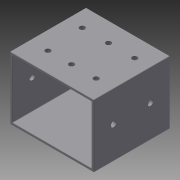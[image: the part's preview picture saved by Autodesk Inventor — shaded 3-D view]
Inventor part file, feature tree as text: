
AUTODESK INVENTOR PART (.ipt)
format: ipt  version: 2014 (Build 180170000, 170)  size: 178,176 bytes
history: native  units: in
note: dims shown in document units (in); Inventor stores cm internally (conversion verified against a paired STEP export)
features: extrude x4, sketch x3, shell x1, fillet x1
ambient origin geometry x8: Origin, YZ Plane, XZ Plane, XY Plane, X Axis, Y Axis, Z Axis, Center Point
bodies: Solid1 (feature_tree)
feature tree (9):
  extrude  "Extrusion1"  Depth=0.5in
  shell  "Shell1"  Thickness=3.0in
  fillet  "Fillet1"  Radius=3.0in
  extrude  "Extrusion6"  Depth=1.8125in
  sketch  "Sketch10"  dims[d87=0.0in d106=0.5in d107=0.5in d108=1.8125in d109=1.8125in d110=3.0in d111=3.0in d112=0.5in d113=0.5in d114=0.5in d115=1.8125in d116=1.8125in d117=1.8125in d118=0.5in d119=0.5in d120=0.5in d126=1.8125in d127=1.8125in d128=1.8125in d130=0.25in d131=0.0in d132=0.25in d133=0.0in d134=1.6in d135=4.2in]
  extrude  "Extrusion7"  Depth=0.25in
  extrude  "Extrusion8"  Depth=0.25in
  sketch  "Sketch1"  dims[d3=0.0in d81=0.5in d82=3.0in d83=3.0in]
  sketch  "Sketch9"  dims[d84=1.8125in d85=1.8125in]
